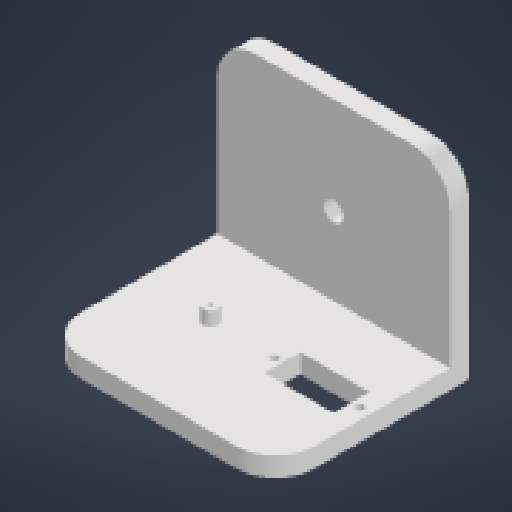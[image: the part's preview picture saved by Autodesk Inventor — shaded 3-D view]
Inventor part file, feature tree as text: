
AUTODESK INVENTOR PART (.ipt)
format: ipt  version: 2023 (Build 270158000, 158)  size: 163,328 bytes
history: native  units: in
note: dims shown in document units (in); Inventor stores cm internally (conversion verified against a paired STEP export)
features: reference x10, extrude x5, sketch x5, other x3, plane x2, fillet x1
ambient origin geometry x8: Origin, YZ Plane, XZ Plane, XY Plane, X Axis, Y Axis, Z Axis, Center Point
bodies: Solid1 (feature_tree)
feature tree (26):
  extrude  "Extrusion1"  Depth=2.5in
  extrude  "Extrusion2"  Depth=0.25in
  fillet  "Fillet1"  Radius=2.25in
  extrude  "Extrusion3"  Depth=0.25in
  extrude  "Extrusion4"  Depth=0.892in
  sketch  "Sketch5"  dims[d12=1.0in d13=0.0in d14=0.19in d18=1.0in d19=0.0in]
  plane  "Work Plane1"
  plane  "Work Plane2"
  extrude  "Extrusion5"  Depth=1.0in
  sketch  "Sketch1"  dims[d0=3.0in d1=2.5in]
  sketch  "Sketch2"  dims[d2=0.25in d3=0.0in d4=0.25in d5=2.25in d6=0.0in]
  sketch  "Sketch3"  dims[d7=0.5in d8=0.25in]
  sketch  "Sketch4"  dims[d9=1.0in d10=0.0in d11=0.892in]
  reference  "Reference1"
  reference  "Reference2"
  reference  "Reference3"
  reference  "Reference4"
  reference  "Reference5"
  reference  "Reference6"
  reference  "Reference7"
  reference  "Reference8"
  reference  "Reference9"
  reference  "Reference10"
  parser-record x1  (decoder bookkeeping rows leaked as tree rows — omitted from the tree; the rows remain in map.json)
  other  "Gripper.iam"
  other  "Servo:1"
note: 1 file-system path scrubbed to <path> (originals preserved in map.json)
